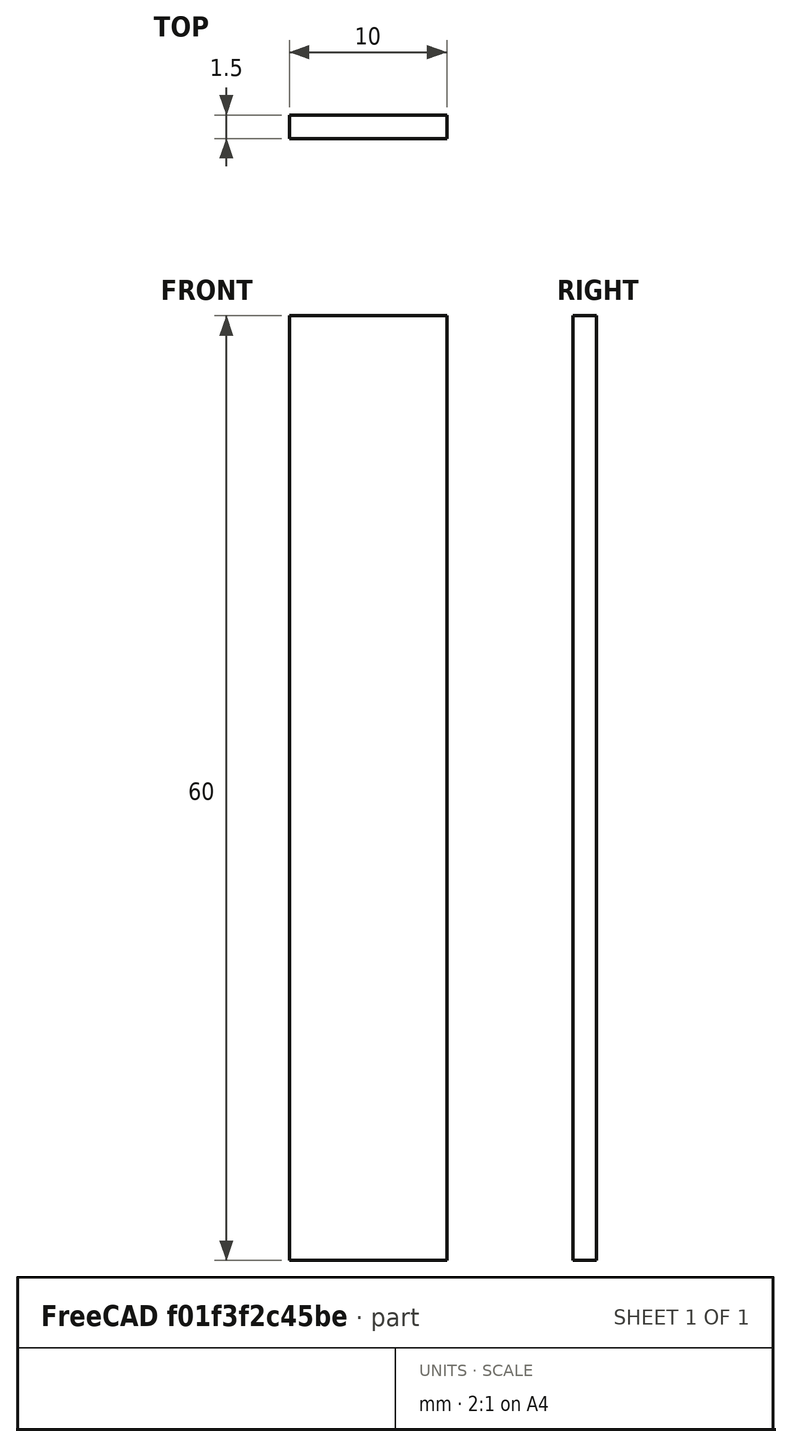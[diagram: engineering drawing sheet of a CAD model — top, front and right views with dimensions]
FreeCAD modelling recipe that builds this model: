
FCSTD DOCUMENT  (FreeCAD 0.14R3700 (Git))
Label: BIRR_PCB_lateral
License: CC-BY 3.0
LicenseURL: http://creativecommons.org/licenses/by/3.0/
objects: Sketcher::SketchObject×1, Part::Extrusion×1, Part::Feature×1
note: 3 computed .brp shape members not serialized (recipe doc carries the construction recipe); baked Part::Feature solids carry a one-line shape summary decoded from their .brp

FEATURE [Sketcher::SketchObject] Sketch  label="PCB_lateral"
  Placement = pos=(0,0,0) rot=(1,0,0;1.5708rad)
  sketch-geometry (4):
    g0: LineSegment StartX=-5 StartY=60 StartZ=0 EndX=5 EndY=60 EndZ=0
    g1: LineSegment StartX=5 StartY=60 StartZ=0 EndX=5 EndY=0 EndZ=0
    g2: LineSegment StartX=5 StartY=0 StartZ=0 EndX=-5 EndY=0 EndZ=0
    g3: LineSegment StartX=-5 StartY=0 StartZ=0 EndX=-5 EndY=60 EndZ=0
  constraints (12):
    c: Coincident(g0,g1)
    c: Coincident(g1,g2)
    c: Coincident(g2,g3)
    c: Coincident(g3,g0)
    c: Horizontal(g0)
    c: Horizontal(g2)
    c: Vertical(g1)
    c: Vertical(g3)
    c: Symmetric(g2,g1,g-2)
    c: DistanceY(g3) = 60
    c: DistanceX(g2) = -10
    c: PointOnObject(g2,g-1)
FEATURE [Part::Extrusion] Extrude
  Base = -> Sketch
  Dir = (0,1.5,0)
  Solid = true
FEATURE [Part::Feature] Extrude001  label="PCB_lateral_copy"
  shape: bbox 10 x 1.5 x 60 mm, 6 faces (baked)
